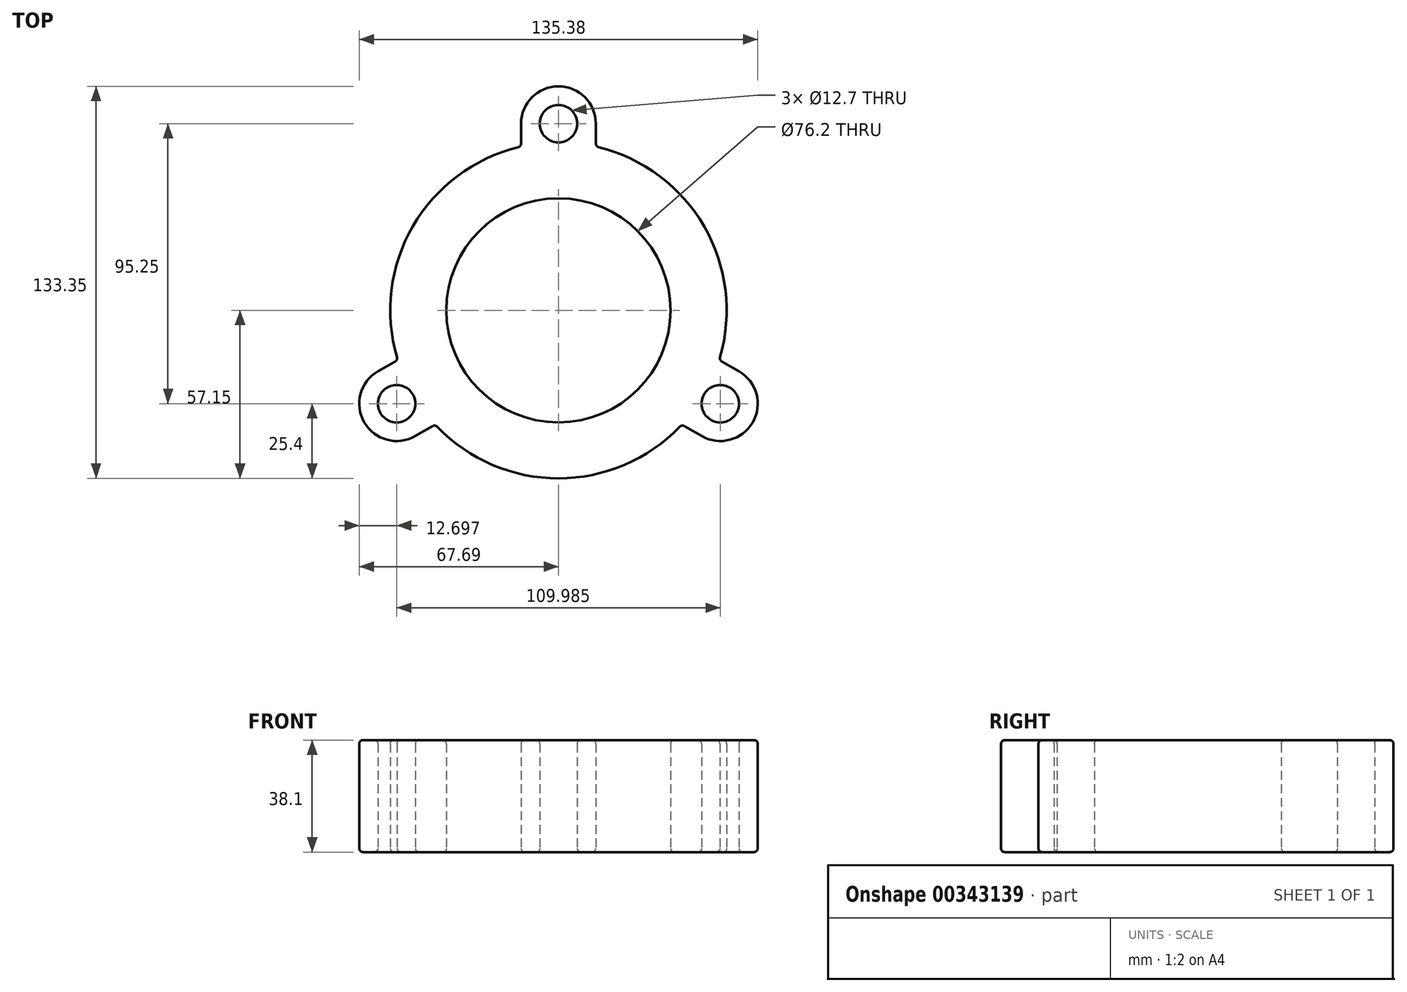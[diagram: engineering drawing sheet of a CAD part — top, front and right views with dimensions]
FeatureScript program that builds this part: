
annotation { "Feature Type Name" : "Feature", "Feature Type Description" : "" }
export const myFeature = defineFeature(function(context is Context, id is Id, definition is map)
    precondition{}
    {
        {
            var Q0;
            Q0=qCreatedBy(makeId("Top.planeOp"),FACE);
            var sketch = newSketch(context, id + "F0", { "sketchPlane" : qUnion([Q0])});
            skCircle(sketch, "E0", {"center": v(0, 0) * mm, "radius": 38.1 * mm});
            skCircle(sketch, "E1", {"center": v(0, 0) * mm, "radius": 63.5 * mm, "construction": true});
            skCircle(sketch, "E2", {"center": v(0, 63.5) * mm, "radius": 6.35 * mm});
            skArc(sketch, "E3", {"start": v(-13.67, 55.5) * mm, "mid": v(-49.5, 28.57) * mm, "end": v(-54.9, -15.91) * mm});
            skLineSegment(sketch, "E4", {"start": v(-12.7, 56.73) * mm, "end": v(-12.7, 63.5) * mm});
            skLineSegment(sketch, "E5", {"start": v(0, 76.2) * mm, "end": v(0, 76.2) * mm});
            skLineSegment(sketch, "E6", {"start": v(12.7, 63.5) * mm, "end": v(12.7, 56.73) * mm});
            skLineSegment(sketch, "E7", {"start": v(0, 0) * mm, "end": v(0, 76.2) * mm, "construction": true});
            skPoint(sketch, "E8.visualSharp", {"position": v(-12.7, 76.2) * mm});
            skArc(sketch, "E8.filletArc", {"start": v(0, 76.2) * mm, "mid": v(-8.98, 72.48) * mm, "end": v(-12.7, 63.5) * mm});
            skPoint(sketch, "E9.visualSharp", {"position": v(12.7, 76.2) * mm});
            skArc(sketch, "E9.filletArc", {"start": v(12.7, 63.5) * mm, "mid": v(8.98, 72.48) * mm, "end": v(0, 76.2) * mm});
            skLineSegment(sketch, "E10.1.0", {"start": v(55.48, -17.36) * mm, "end": v(61.34, -20.75) * mm});
            skArc(sketch, "E10.1.1", {"start": v(66, -38.1) * mm, "mid": v(67.26, -28.46) * mm, "end": v(61.34, -20.75) * mm});
            skArc(sketch, "E10.1.2", {"start": v(48.64, -42.75) * mm, "mid": v(58.28, -44.02) * mm, "end": v(66, -38.1) * mm});
            skCircle(sketch, "E10.1.3", {"center": v(55, -31.75) * mm, "radius": 6.35 * mm});
            skLineSegment(sketch, "E10.1.4", {"start": v(48.64, -42.75) * mm, "end": v(42.78, -39.36) * mm});
            skLineSegment(sketch, "E10.2.0", {"start": v(-42.78, -39.36) * mm, "end": v(-48.64, -42.75) * mm});
            skArc(sketch, "E10.2.1", {"start": v(-66, -38.1) * mm, "mid": v(-58.28, -44.02) * mm, "end": v(-48.64, -42.75) * mm});
            skArc(sketch, "E10.2.2", {"start": v(-61.34, -20.75) * mm, "mid": v(-67.26, -28.46) * mm, "end": v(-66, -38.1) * mm});
            skCircle(sketch, "E10.2.3", {"center": v(-55, -31.75) * mm, "radius": 6.35 * mm});
            skLineSegment(sketch, "E10.2.4", {"start": v(-61.34, -20.75) * mm, "end": v(-55.48, -17.36) * mm});
            skLineSegment(sketch, "E10.anchor1", {"start": v(0, 0) * mm, "end": v(0, 63.5) * mm, "construction": true});
            skLineSegment(sketch, "E10.anchor2", {"start": v(0, 0) * mm, "end": v(-55, -31.75) * mm, "construction": true});
            skArc(sketch, "E11.trimOffspring", {"start": v(-41.22, -39.58) * mm, "mid": v(0, -57.15) * mm, "end": v(41.22, -39.58) * mm});
            skArc(sketch, "E12.trimOffspring", {"start": v(54.9, -15.91) * mm, "mid": v(49.5, 28.58) * mm, "end": v(13.67, 55.5) * mm});
            skPoint(sketch, "E13.visualSharp", {"position": v(12.7, 55.72) * mm});
            skArc(sketch, "E13.filletArc", {"start": v(12.7, 56.73) * mm, "mid": v(12.97, 55.94) * mm, "end": v(13.67, 55.5) * mm});
            skPoint(sketch, "E14.visualSharp", {"position": v(-12.7, 55.72) * mm});
            skArc(sketch, "E14.filletArc", {"start": v(-13.67, 55.5) * mm, "mid": v(-12.97, 55.94) * mm, "end": v(-12.7, 56.73) * mm});
            skPoint(sketch, "E15.visualSharp", {"position": v(54.6, -16.86) * mm});
            skArc(sketch, "E15.filletArc", {"start": v(54.9, -15.91) * mm, "mid": v(54.93, -16.74) * mm, "end": v(55.48, -17.36) * mm});
            skPoint(sketch, "E16.visualSharp", {"position": v(41.9, -38.86) * mm});
            skArc(sketch, "E16.filletArc", {"start": v(42.78, -39.36) * mm, "mid": v(41.96, -39.2) * mm, "end": v(41.22, -39.58) * mm});
            skPoint(sketch, "E17.visualSharp", {"position": v(-41.9, -38.86) * mm});
            skArc(sketch, "E17.filletArc", {"start": v(-41.22, -39.58) * mm, "mid": v(-41.96, -39.2) * mm, "end": v(-42.78, -39.36) * mm});
            skPoint(sketch, "E18.visualSharp", {"position": v(-54.6, -16.86) * mm});
            skArc(sketch, "E18.filletArc", {"start": v(-55.48, -17.36) * mm, "mid": v(-54.93, -16.74) * mm, "end": v(-54.9, -15.91) * mm});
            skSolve(sketch);
        }
        {
            var Q0;
            Q0 = qSketchRegion(id + "F0", true);
            extrude(context, id + "F1", {"entities" : qUnion([Q0]), "depth" : 38.1 * mm});
        }
        {
            var Q0;
            Q0=makeQuery(id+"F1.opExtrude","CAP_FACE",FACE,{"disambiguationData":[OSD([sQuery(id+"F0.wireOp",EDGE,"E0"),sQuery(id+"F0.wireOp",EDGE,"E2"),sQuery(id+"F0.wireOp",EDGE,"E3"),sQuery(id+"F0.wireOp",EDGE,"E4"),sQuery(id+"F0.wireOp",EDGE,"E6"),sQuery(id+"F0.wireOp",EDGE,"E8.filletArc"),sQuery(id+"F0.wireOp",EDGE,"E9.filletArc"),sQuery(id+"F0.wireOp",EDGE,"E10.1.0"),sQuery(id+"F0.wireOp",EDGE,"E10.1.1"),sQuery(id+"F0.wireOp",EDGE,"E10.1.2"),sQuery(id+"F0.wireOp",EDGE,"E10.1.3"),sQuery(id+"F0.wireOp",EDGE,"E10.1.4"),sQuery(id+"F0.wireOp",EDGE,"E10.2.0"),sQuery(id+"F0.wireOp",EDGE,"E10.2.1"),sQuery(id+"F0.wireOp",EDGE,"E10.2.2"),sQuery(id+"F0.wireOp",EDGE,"E10.2.3"),sQuery(id+"F0.wireOp",EDGE,"E10.2.4"),sQuery(id+"F0.wireOp",EDGE,"E11.trimOffspring"),sQuery(id+"F0.wireOp",EDGE,"E12.trimOffspring")])],"isStart":false});
            var Q1;
            Q1=makeQuery(id+"F1.opExtrude","CAP_FACE",FACE,{"disambiguationData":[OSD([sQuery(id+"F0.wireOp",EDGE,"E0"),sQuery(id+"F0.wireOp",EDGE,"E2"),sQuery(id+"F0.wireOp",EDGE,"E3"),sQuery(id+"F0.wireOp",EDGE,"E4"),sQuery(id+"F0.wireOp",EDGE,"E6"),sQuery(id+"F0.wireOp",EDGE,"E8.filletArc"),sQuery(id+"F0.wireOp",EDGE,"E9.filletArc"),sQuery(id+"F0.wireOp",EDGE,"E10.1.0"),sQuery(id+"F0.wireOp",EDGE,"E10.1.1"),sQuery(id+"F0.wireOp",EDGE,"E10.1.2"),sQuery(id+"F0.wireOp",EDGE,"E10.1.3"),sQuery(id+"F0.wireOp",EDGE,"E10.1.4"),sQuery(id+"F0.wireOp",EDGE,"E10.2.0"),sQuery(id+"F0.wireOp",EDGE,"E10.2.1"),sQuery(id+"F0.wireOp",EDGE,"E10.2.2"),sQuery(id+"F0.wireOp",EDGE,"E10.2.3"),sQuery(id+"F0.wireOp",EDGE,"E10.2.4"),sQuery(id+"F0.wireOp",EDGE,"E11.trimOffspring"),sQuery(id+"F0.wireOp",EDGE,"E12.trimOffspring")])],"isStart":true});
            fillet(context, id + "F2", {"entities" : qUnion([Q0, Q1]), "radius" : 1.27 * mm, "tangentPropagation" : true, "allowEdgeOverflow" : false});
        }
    });
